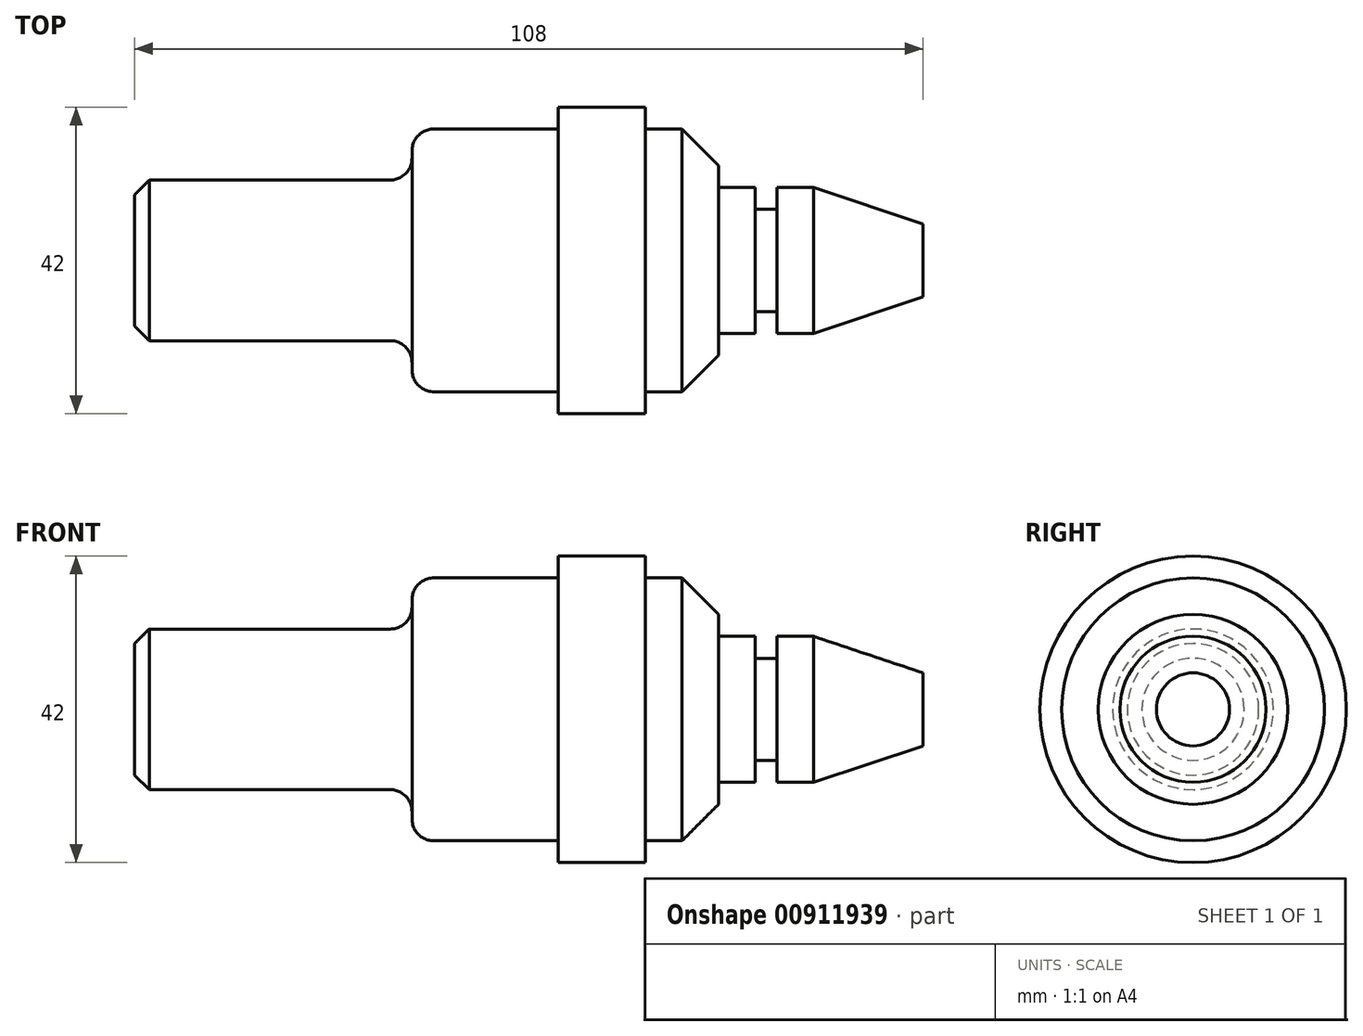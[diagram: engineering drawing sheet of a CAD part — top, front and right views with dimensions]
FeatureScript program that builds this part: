
annotation { "Feature Type Name" : "Feature", "Feature Type Description" : "" }
export const myFeature = defineFeature(function(context is Context, id is Id, definition is map)
    precondition{}
    {
        {
            var Q0;
            Q0=qCreatedBy(makeId("Top.planeOp"),FACE);
            var sketch = newSketch(context, id + "F0", { "sketchPlane" : qUnion([Q0])});
            skLineSegment(sketch, "E0", {"start": v(-39.66, 0) * mm, "end": v(68.34, 0) * mm});
            skLineSegment(sketch, "E1", {"start": v(-39.66, 0) * mm, "end": v(-39.66, -11) * mm});
            skLineSegment(sketch, "E2", {"start": v(-39.66, -11) * mm, "end": v(-1.66, -11) * mm});
            skLineSegment(sketch, "E3", {"start": v(-1.66, -11) * mm, "end": v(-1.66, -18) * mm});
            skLineSegment(sketch, "E4", {"start": v(-1.66, -18) * mm, "end": v(18.34, -18) * mm});
            skLineSegment(sketch, "E5", {"start": v(18.34, -18) * mm, "end": v(18.34, -21) * mm});
            skLineSegment(sketch, "E6", {"start": v(18.34, -21) * mm, "end": v(30.34, -21) * mm});
            skLineSegment(sketch, "E7", {"start": v(30.34, -21) * mm, "end": v(30.34, -18) * mm});
            skLineSegment(sketch, "E8", {"start": v(30.34, -18) * mm, "end": v(40.34, -18) * mm});
            skLineSegment(sketch, "E9", {"start": v(40.34, -18) * mm, "end": v(40.34, -10) * mm});
            skLineSegment(sketch, "E10", {"start": v(40.34, -10) * mm, "end": v(45.34, -10) * mm});
            skLineSegment(sketch, "E11", {"start": v(45.34, -10) * mm, "end": v(45.34, -7) * mm});
            skLineSegment(sketch, "E12", {"start": v(45.34, -7) * mm, "end": v(48.34, -7) * mm});
            skLineSegment(sketch, "E13", {"start": v(48.34, -7) * mm, "end": v(48.34, -10) * mm});
            skLineSegment(sketch, "E14", {"start": v(48.34, -10) * mm, "end": v(53.34, -10) * mm});
            skLineSegment(sketch, "E15", {"start": v(53.34, -10) * mm, "end": v(68.34, -5) * mm});
            skLineSegment(sketch, "E16", {"start": v(68.34, 0) * mm, "end": v(68.34, -5) * mm});
            skSolve(sketch);
        }
        {
            var Q0;
            Q0=makeQuery(id+"F0.imprint","IMPRINT",FACE,{"disambiguationData":[TD([[makeQuery(id+"F0.imprint","IMPRINT",EDGE,{"derivedFrom":sQuery(id+"F0.wireOp",EDGE,"E0")}),-1.0]])]});
            var Q1;
            Q1=sQuery(id+"F0.wireOp",EDGE,"E0");
            revolve(context, id + "F1", {"surfaceOperationType" : NewSurfaceOperationType.NEW, "entities" : qUnion([Q0]), "axis" : qUnion([Q1]), "revolveType" : RevolveType.FULL});
        }
        {
            var Q0;
            Q0=makeQuery(id+"F1.opRevolve","SWEPT_EDGE",EDGE,{"disambiguationData":[OSD([sQuery(id+"F0.wireOp",EDGE,"E1"),sQuery(id+"F0.wireOp",EDGE,"E2")])]});
            chamfer(context, id + "F2", {"entities" : qUnion([Q0]), "chamferType" : ChamferType.OFFSET_ANGLE, "width" : 2 * mm, "oppositeDirection" : false, "angle" : 45 * degree, "tangentPropagation" : true});
        }
        {
            var Q0;
            Q0=makeQuery(id+"F1.opRevolve","SWEPT_EDGE",EDGE,{"disambiguationData":[OSD([sQuery(id+"F0.wireOp",EDGE,"E3"),sQuery(id+"F0.wireOp",EDGE,"E4")])]});
            var Q1;
            Q1=makeQuery(id+"F1.opRevolve","SWEPT_EDGE",EDGE,{"disambiguationData":[OSD([sQuery(id+"F0.wireOp",EDGE,"E2"),sQuery(id+"F0.wireOp",EDGE,"E3")])]});
            fillet(context, id + "F3", {"entities" : qUnion([Q0, Q1]), "radius" : 3 * mm, "tangentPropagation" : true, "allowEdgeOverflow" : false});
        }
        {
            var Q0;
            Q0=makeQuery(id+"F1.opRevolve","SWEPT_EDGE",EDGE,{"disambiguationData":[OSD([sQuery(id+"F0.wireOp",EDGE,"E8"),sQuery(id+"F0.wireOp",EDGE,"E9")])]});
            chamfer(context, id + "F4", {"entities" : qUnion([Q0]), "width" : 5 * mm, "tangentPropagation" : true});
        }
    });
